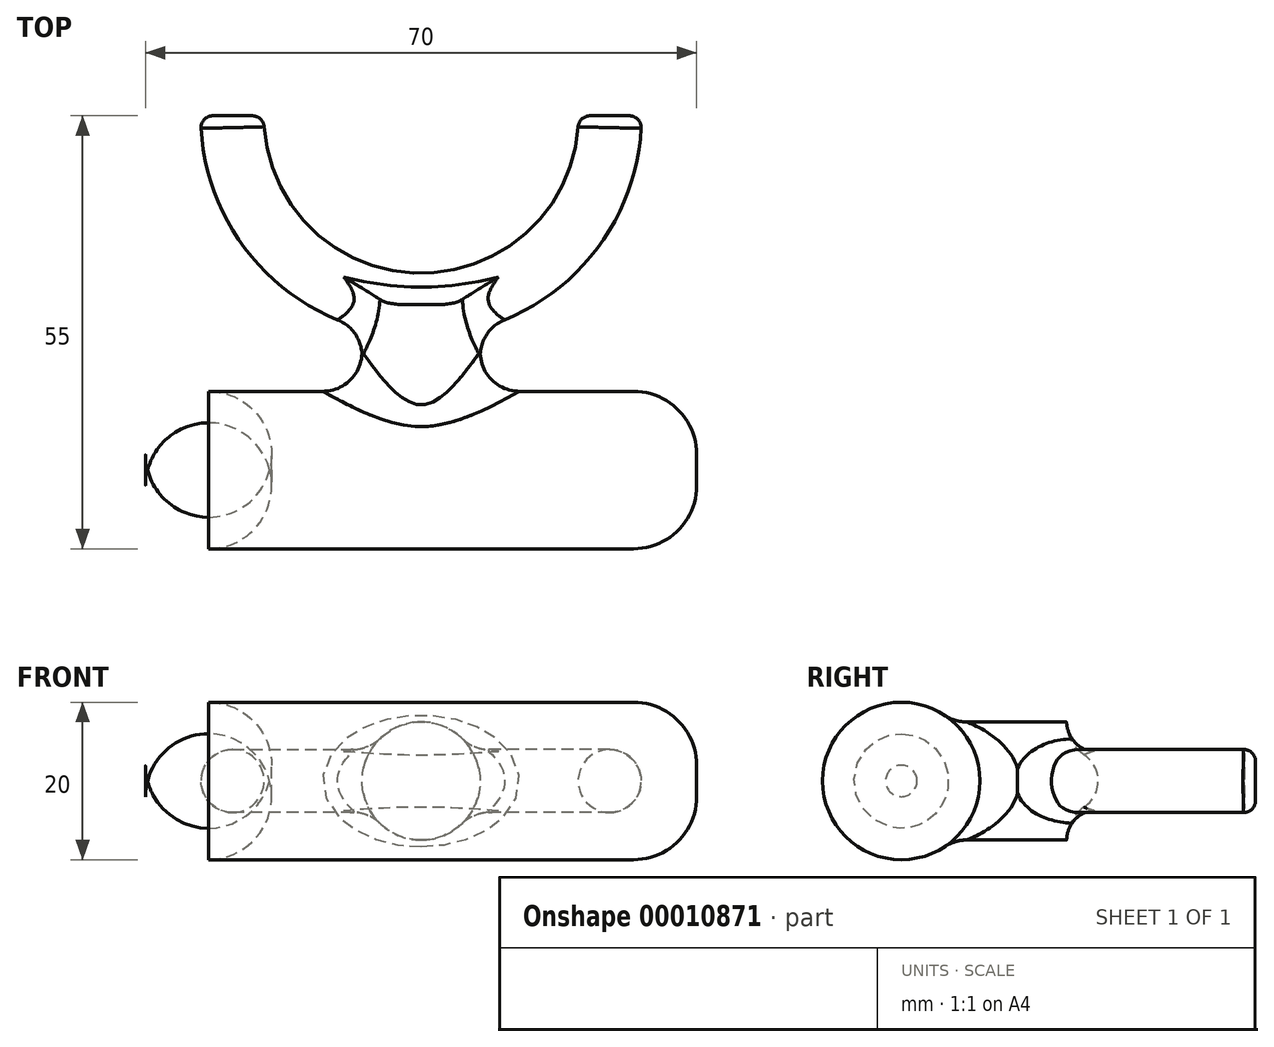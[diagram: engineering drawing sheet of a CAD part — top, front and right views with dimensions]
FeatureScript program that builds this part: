
annotation { "Feature Type Name" : "Feature", "Feature Type Description" : "" }
export const myFeature = defineFeature(function(context is Context, id is Id, definition is map)
    precondition{}
    {
        {
            var Q0;
            Q0=qCreatedBy(makeId("Top.planeOp"),FACE);
            var sketch = newSketch(context, id + "F0", { "sketchPlane" : qUnion([Q0])});
            skLineSegment(sketch, "E0", {"start": v(0, 0) * mm, "end": v(-70, 0) * mm});
            skLineSegment(sketch, "E1", {"start": v(-35, 0) * mm, "end": v(-35, 21) * mm});
            skArc(sketch, "E2", {"start": v(-59, 45) * mm, "mid": v(-35, 21) * mm, "end": v(-11, 45) * mm});
            skLineSegment(sketch, "E3", {"start": v(-35, 21) * mm, "end": v(-35, 45) * mm});
            skSolve(sketch);
        }
        {
            var Q0;
            Q0=qCreatedBy(makeId("Right.planeOp"),FACE);
            var sketch = newSketch(context, id + "F1", { "sketchPlane" : qUnion([Q0])});
            skCircle(sketch, "E4", {"center": v(0, 0) * mm, "radius": 10 * mm});
            skSolve(sketch);
        }
        {
            var Q0;
            Q0=qCreatedBy(makeId("Top.planeOp"),FACE);
            var sketch = newSketch(context, id + "F2", { "sketchPlane" : qUnion([Q0])});
            skLineSegment(sketch, "E5", {"start": v(0, 0) * mm, "end": v(-70, 0) * mm});
            skSolve(sketch);
        }
        {
            var Q0;
            Q0=makeQuery(id+"F1.imprint","IMPRINT",FACE,{"disambiguationData":[TD([[makeQuery(id+"F1.imprint","IMPRINT",EDGE,{"derivedFrom":sQuery(id+"F1.wireOp",EDGE,"E4")}),1.0]])]});
            var Q1;
            Q1 = qBodyType(qCreatedBy(id + "F2" ,EDGE), BodyType.WIRE);
            sweep(context, id + "F3", {"profiles" : qUnion([Q0]), "path" : qUnion([Q1])});
        }
        {
            var Q0;
            Q0=sQuery(id+"F0.wireOp",EDGE,"E1");
            var Q1;
            Q1=sQuery(id+"F0.wireOp",VERTEX,"E1.end");
            cPlane(context, id + "F4", {"entities" : qUnion([Q0, Q1]), "cplaneType" : CPlaneType.LINE_POINT, "offset" : 150 * mm, "width" : 150 * mm, "height" : 150 * mm});
        }
        {
            var Q0;
            Q0=qCreatedBy(id+"F4.planeOp",FACE);
            var sketch = newSketch(context, id + "F5", { "sketchPlane" : qUnion([Q0])});
            skCircle(sketch, "E6", {"center": v(35, 0) * mm, "radius": 7.5 * mm});
            skSolve(sketch);
        }
        {
            var Q0;
            Q0=makeQuery(id+"F5.imprint","IMPRINT",FACE,{"disambiguationData":[TD([[makeQuery(id+"F5.imprint","IMPRINT",EDGE,{"derivedFrom":sQuery(id+"F5.wireOp",EDGE,"E6")}),1.0]])]});
            var Q1;
            Q1=sQuery(id+"F0.wireOp",EDGE,"E1");
            sweep(context, id + "F6", {"operationType" : NewBodyOperationType.ADD, "profiles" : qUnion([Q0]), "path" : qUnion([Q1])});
        }
        {
            var Q0;
            Q0=sQuery(id+"F0.wireOp",EDGE,"E3");
            var Q1;
            Q1=sQuery(id+"F0.wireOp",VERTEX,"E2.center");
            cPlane(context, id + "F7", {"entities" : qUnion([Q0, Q1]), "cplaneType" : CPlaneType.LINE_POINT, "offset" : 150 * mm, "width" : 150 * mm, "height" : 150 * mm});
        }
        {
            var Q0;
            Q0=qCreatedBy(id+"F7.planeOp",FACE);
            var sketch = newSketch(context, id + "F8", { "sketchPlane" : qUnion([Q0])});
            skLineSegment(sketch, "E7", {"start": v(0, 0) * mm, "end": v(11, 0) * mm});
            skCircle(sketch, "E8", {"center": v(11, 0) * mm, "radius": 4 * mm});
            skSolve(sketch);
        }
        {
            var Q0;
            Q0=makeQuery(id+"F8.imprint","IMPRINT",FACE,{"disambiguationData":[TD([[makeQuery(id+"F8.imprint","IMPRINT",EDGE,{"derivedFrom":sQuery(id+"F8.wireOp",EDGE,"E8")}),1.0]])]});
            var Q1;
            Q1=sQuery(id+"F0.wireOp",EDGE,"E2");
            sweep(context, id + "F9", {"operationType" : NewBodyOperationType.ADD, "profiles" : qUnion([Q0]), "path" : qUnion([Q1])});
        }
        {
            var Q0;
            Q0=makeQuery(id+"F9.boolean.opBoolean","INTERSECT",EDGE,{"disambiguationData":[OD(1.0)],"derivedFrom":[makeQuery(id+"F6.opSweep","CAP_FACE",FACE,{"disambiguationData":[OSD([sQuery(id+"F0.wireOp",VERTEX,"E1.end"),sQuery(id+"F5.wireOp",EDGE,"E6")])],"isStart":true}),makeQuery(id+"F9.opSweep","SWEPT_FACE",FACE,{"disambiguationData":[OSD([sQuery(id+"F0.wireOp",EDGE,"E2"),sQuery(id+"F8.wireOp",EDGE,"E8")])]})]});
            var Q1;
            Q1=makeQuery(id+"F9.boolean.opBoolean","INTERSECT",EDGE,{"disambiguationData":[OD(0.0)],"derivedFrom":[makeQuery(id+"F6.opSweep","SWEPT_FACE",FACE,{"disambiguationData":[OSD([sQuery(id+"F0.wireOp",EDGE,"E1"),sQuery(id+"F5.wireOp",EDGE,"E6")])]}),makeQuery(id+"F9.opSweep","SWEPT_FACE",FACE,{"disambiguationData":[OSD([sQuery(id+"F0.wireOp",EDGE,"E2"),sQuery(id+"F8.wireOp",EDGE,"E8")])]})]});
            var Q2;
            Q2=makeQuery(id+"F9.boolean.opBoolean","INTERSECT",EDGE,{"disambiguationData":[OD(0.0)],"derivedFrom":[makeQuery(id+"F6.opSweep","CAP_FACE",FACE,{"disambiguationData":[OSD([sQuery(id+"F0.wireOp",VERTEX,"E1.end"),sQuery(id+"F5.wireOp",EDGE,"E6")])],"isStart":true}),makeQuery(id+"F9.opSweep","SWEPT_FACE",FACE,{"disambiguationData":[OSD([sQuery(id+"F0.wireOp",EDGE,"E2"),sQuery(id+"F8.wireOp",EDGE,"E8")])]})]});
            var Q3;
            Q3=makeQuery(id+"F9.boolean.opBoolean","INTERSECT",EDGE,{"disambiguationData":[OD(1.0)],"derivedFrom":[makeQuery(id+"F6.opSweep","SWEPT_FACE",FACE,{"disambiguationData":[OSD([sQuery(id+"F0.wireOp",EDGE,"E1"),sQuery(id+"F5.wireOp",EDGE,"E6")])]}),makeQuery(id+"F9.opSweep","SWEPT_FACE",FACE,{"disambiguationData":[OSD([sQuery(id+"F0.wireOp",EDGE,"E2"),sQuery(id+"F8.wireOp",EDGE,"E8")])]})]});
            fillet(context, id + "F10", {"entities" : qUnion([Q0, Q1, Q2, Q3]), "radius" : 5 * mm, "tangentPropagation" : true, "allowEdgeOverflow" : false});
        }
        {
            var Q0;
            Q0=makeQuery(id+"F9.opSweep","CAP_FACE",FACE,{"disambiguationData":[OSD([sQuery(id+"F0.wireOp",VERTEX,"E2.start"),sQuery(id+"F8.wireOp",EDGE,"E8")])],"isStart":false});
            var Q1;
            Q1=makeQuery(id+"F9.opSweep","CAP_FACE",FACE,{"disambiguationData":[OSD([sQuery(id+"F0.wireOp",VERTEX,"E2.end"),sQuery(id+"F8.wireOp",EDGE,"E8")])],"isStart":true});
            fillet(context, id + "F11", {"entities" : qUnion([Q0, Q1]), "radius" : 1.5 * mm, "tangentPropagation" : true, "allowEdgeOverflow" : false});
        }
        {
            var Q0;
            Q0=makeQuery(id+"F3.opSweep","CAP_EDGE",EDGE,{"disambiguationData":[OSD([sQuery(id+"F1.wireOp",EDGE,"E4"),sQuery(id+"F2.wireOp",VERTEX,"E5.start")])],"isStart":true});
            var Q1;
            Q1=makeQuery(id+"F3.opSweep","CAP_EDGE",EDGE,{"disambiguationData":[OSD([sQuery(id+"F1.wireOp",EDGE,"E4"),sQuery(id+"F2.wireOp",VERTEX,"E5.end")])],"isStart":false});
            fillet(context, id + "F12", {"entities" : qUnion([Q0, Q1]), "radius" : 8 * mm, "tangentPropagation" : true, "allowEdgeOverflow" : false});
        }
        {
            var Q0;
            Q0=makeQuery(id+"F6.boolean.opBoolean","INTERSECT",EDGE,{"derivedFrom":[makeQuery(id+"F3.opSweep","SWEPT_FACE",FACE,{"disambiguationData":[OSD([sQuery(id+"F1.wireOp",EDGE,"E4"),sQuery(id+"F2.wireOp",EDGE,"E5")])]}),makeQuery(id+"F6.opSweep","SWEPT_FACE",FACE,{"disambiguationData":[OSD([sQuery(id+"F0.wireOp",EDGE,"E1"),sQuery(id+"F5.wireOp",EDGE,"E6")])]})]});
            fillet(context, id + "F13", {"entities" : qUnion([Q0]), "radius" : 5 * mm, "tangentPropagation" : true, "allowEdgeOverflow" : false});
        }
    });
